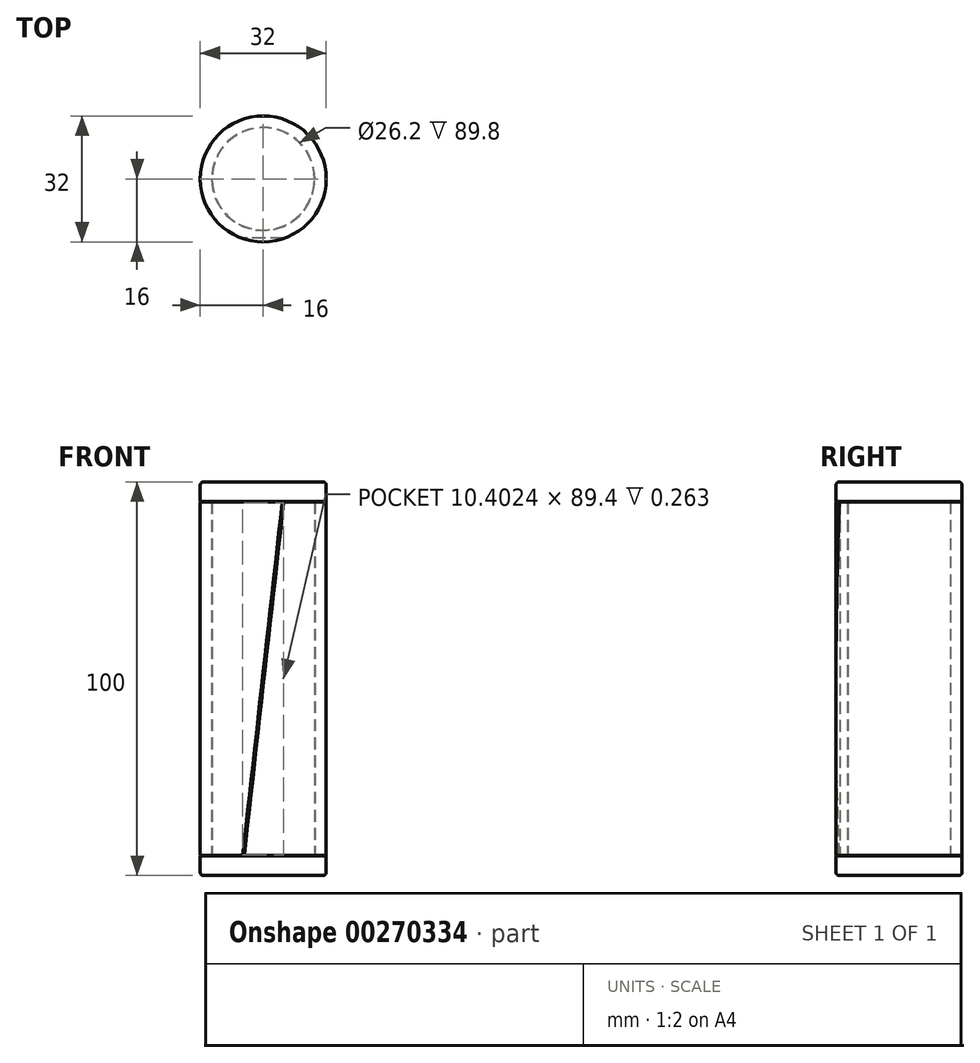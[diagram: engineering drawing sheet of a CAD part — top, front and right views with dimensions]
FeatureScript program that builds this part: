
annotation { "Feature Type Name" : "Feature", "Feature Type Description" : "" }
export const myFeature = defineFeature(function(context is Context, id is Id, definition is map)
    precondition{}
    {
        {
            var Q0;
            Q0=qCreatedBy(makeId("Front.planeOp"),FACE);
            var sketch = newSketch(context, id + "F0", { "sketchPlane" : qUnion([Q0])});
            skLineSegment(sketch, "E0", {"start": v(0, 0) * mm, "end": v(0, 100) * mm});
            skLineSegment(sketch, "E1", {"start": v(0, 100) * mm, "end": v(16, 100) * mm});
            skLineSegment(sketch, "E2", {"start": v(0, 0) * mm, "end": v(16, 0) * mm});
            skLineSegment(sketch, "E3", {"start": v(16, 100) * mm, "end": v(16, 95) * mm});
            skLineSegment(sketch, "E4", {"start": v(16, 95) * mm, "end": v(13, 95) * mm});
            skLineSegment(sketch, "E5", {"start": v(13, 95) * mm, "end": v(13, 5) * mm});
            skLineSegment(sketch, "E6", {"start": v(13, 5) * mm, "end": v(16, 5) * mm});
            skLineSegment(sketch, "E7", {"start": v(16, 5) * mm, "end": v(16, 0) * mm});
            skSolve(sketch);
        }
        {
            var Q0;
            Q0 = qSketchRegion(id + "F0", true);
            var Q1;
            Q1=sQuery(id+"F0.wireOp",EDGE,"E0");
            revolve(context, id + "F1", {"entities" : qUnion([Q0]), "axis" : qUnion([Q1]), "revolveType" : RevolveType.FULL});
        }
        {
            var Q0;
            Q0=qCreatedBy(makeId("Front.planeOp"),FACE);
            var sketch = newSketch(context, id + "F2", { "sketchPlane" : qUnion([Q0])});
            skLineSegment(sketch, "E8", {"start": v(16, 94.9) * mm, "end": v(13.1, 94.9) * mm});
            skLineSegment(sketch, "E9", {"start": v(13.1, 94.9) * mm, "end": v(13.1, 5.1) * mm});
            skLineSegment(sketch, "E10", {"start": v(13.1, 5.1) * mm, "end": v(16, 5.1) * mm});
            skLineSegment(sketch, "E11", {"start": v(16, 100) * mm, "end": v(16, 97) * mm});
            skPoint(sketch, "E12.centerSnap0", {"position": v(13.1, 50) * mm});
            skLineSegment(sketch, "E13", {"start": v(16, 94.9) * mm, "end": v(16, 91.9) * mm});
            skLineSegment(sketch, "E14", {"start": v(16, 91.9) * mm, "end": v(16, 91.9) * mm});
            skLineSegment(sketch, "E15", {"start": v(16, 91.9) * mm, "end": v(16, 8.1) * mm});
            skLineSegment(sketch, "E16", {"start": v(16, 8.1) * mm, "end": v(16, 8.1) * mm});
            skLineSegment(sketch, "E17", {"start": v(16, 8.1) * mm, "end": v(16, 5.1) * mm});
            skSolve(sketch);
        }
        {
            var Q0;
            Q0=qCreatedBy(makeId("Front.planeOp"),FACE);
            var sketch = newSketch(context, id + "F3", { "sketchPlane" : qUnion([Q0])});
            skLineSegment(sketch, "E18", {"start": v(0, 0) * mm, "end": v(0, 12.59) * mm});
            skSolve(sketch);
        }
        {
            var Q0;
            Q0=makeQuery(id+"F2.imprint","IMPRINT",FACE,{"disambiguationData":[TD([[makeQuery(id+"F2.imprint","IMPRINT",EDGE,{"derivedFrom":sQuery(id+"F2.wireOp",EDGE,"E8")}),1.0]])]});
            var Q1;
            Q1=sQuery(id+"F3.wireOp",EDGE,"E18");
            revolve(context, id + "F4", {"entities" : qUnion([Q0]), "axis" : qUnion([Q1]), "revolveType" : RevolveType.FULL});
        }
        {
            var Q0;
            Q0=makeQuery(id+"F4.opRevolve","SWEPT_EDGE",EDGE,{"disambiguationData":[OSD([sQuery(id+"F2.wireOp",EDGE,"E13"),sQuery(id+"F2.wireOp",EDGE,"E14")])]});
            var Q1;
            Q1=makeQuery(id+"F4.opRevolve","SWEPT_EDGE",EDGE,{"disambiguationData":[OSD([sQuery(id+"F2.wireOp",EDGE,"E16"),sQuery(id+"F2.wireOp",EDGE,"E17")])]});
            fillet(context, id + "F5", {"entities" : qUnion([Q0, Q1]), "radius" : 0.2 * mm, "tangentPropagation" : true, "allowEdgeOverflow" : false});
        }
        {
            var Q0;
            Q0=makeQuery(id+"F1.opRevolve","SWEPT_EDGE",EDGE,{"disambiguationData":[OSD([sQuery(id+"F0.wireOp",EDGE,"E1"),sQuery(id+"F0.wireOp",EDGE,"E3")])]});
            var Q1;
            Q1=makeQuery(id+"F1.opRevolve","SWEPT_EDGE",EDGE,{"disambiguationData":[OSD([sQuery(id+"F0.wireOp",EDGE,"E2"),sQuery(id+"F0.wireOp",EDGE,"E7")])]});
            fillet(context, id + "F6", {"entities" : qUnion([Q0, Q1]), "radius" : 0.8 * mm, "tangentPropagation" : true, "allowEdgeOverflow" : false});
        }
        {
            var Q0;
            Q0=makeQuery(id+"F1.opRevolve","SWEPT_EDGE",EDGE,{"disambiguationData":[OSD([sQuery(id+"F0.wireOp",EDGE,"E3"),sQuery(id+"F0.wireOp",EDGE,"E4")])]});
            var Q1;
            Q1=makeQuery(id+"F1.opRevolve","SWEPT_EDGE",EDGE,{"disambiguationData":[OSD([sQuery(id+"F0.wireOp",EDGE,"E6"),sQuery(id+"F0.wireOp",EDGE,"E7")])]});
            fillet(context, id + "F7", {"entities" : qUnion([Q0, Q1]), "radius" : 0.2 * mm, "tangentPropagation" : true, "allowEdgeOverflow" : false});
        }
        {
            var Q0;
            Q0=qCreatedBy(makeId("Front.planeOp"),FACE);
            cPlane(context, id + "F8", {"entities" : qUnion([Q0]), "cplaneType" : CPlaneType.OFFSET, "offset" : 25 * mm, "width" : 150 * mm, "height" : 150 * mm});
        }
        {
            var Q0;
            Q0=qCreatedBy(id+"F8.planeOp",FACE);
            var sketch = newSketch(context, id + "F9", { "sketchPlane" : qUnion([Q0])});
            skLineSegment(sketch, "E19", {"start": v(-16, 5.3) * mm, "end": v(-16, 94.7) * mm});
            skLineSegment(sketch, "E20", {"start": v(16, 94.7) * mm, "end": v(16, 5.3) * mm});
            skLineSegment(sketch, "E21.0", {"start": v(16, 94.7) * mm, "end": v(-16, 94.7) * mm});
            skLineSegment(sketch, "E22.0", {"start": v(-16, 5.3) * mm, "end": v(16, 5.3) * mm});
            skLineSegment(sketch, "E23", {"start": v(5, 94.7) * mm, "end": v(-5, 5.3) * mm});
            skLineSegment(sketch, "E24.0", {"start": v(4.8, 94.72) * mm, "end": v(-5.24, 4.94) * mm});
            skLineSegment(sketch, "E25.0", {"start": v(5.28, 95.37) * mm, "end": v(-4.8, 5.28) * mm});
            skSolve(sketch);
        }
        {
            var Q0;
            {var subQ0=sQuery(id+"F9.wireOp",EDGE,"E23");Q0=makeQuery(id+"F9.imprint","IMPRINT",FACE,{"disambiguationData":[TD([[makeQuery(id+"F9.imprint","IMPRINT",EDGE,{"derivedFrom":subQ0}),1.0]])]});}
            var Q1;
            {var subQ0=sQuery(id+"F9.wireOp",EDGE,"E23");Q1=makeQuery(id+"F9.imprint","IMPRINT",FACE,{"disambiguationData":[TD([[makeQuery(id+"F9.imprint","IMPRINT",EDGE,{"derivedFrom":subQ0}),-1.0]])]});}
            var Q2;
            Q2=makeQuery(id+"F4.opRevolve","SWEPT_FACE",FACE,{"disambiguationData":[OSD([sQuery(id+"F2.wireOp",EDGE,"E13"),sQuery(id+"F2.wireOp",EDGE,"E15"),sQuery(id+"F2.wireOp",EDGE,"E17")])]});
            var Q3;
            Q3=makeQuery(id+"F4.opRevolve","SWEPT_BODY",BODY,{"disambiguationData":[OSD([sQuery(id+"F2.wireOp",EDGE,"E8"),sQuery(id+"F2.wireOp",EDGE,"E9"),sQuery(id+"F2.wireOp",EDGE,"E10"),sQuery(id+"F2.wireOp",EDGE,"E13"),sQuery(id+"F2.wireOp",EDGE,"E15"),sQuery(id+"F2.wireOp",EDGE,"E17")])]});
            extrude(context, id + "F10", {"entities" : qUnion([Q0, Q1]), "operationType" : NewBodyOperationType.REMOVE, "oppositeDirection" : true, "endBoundEntityFace" : qUnion([Q2]), "endBoundEntityBody" : qUnion([Q3]), "depth" : 10 * mm});
        }
    });
